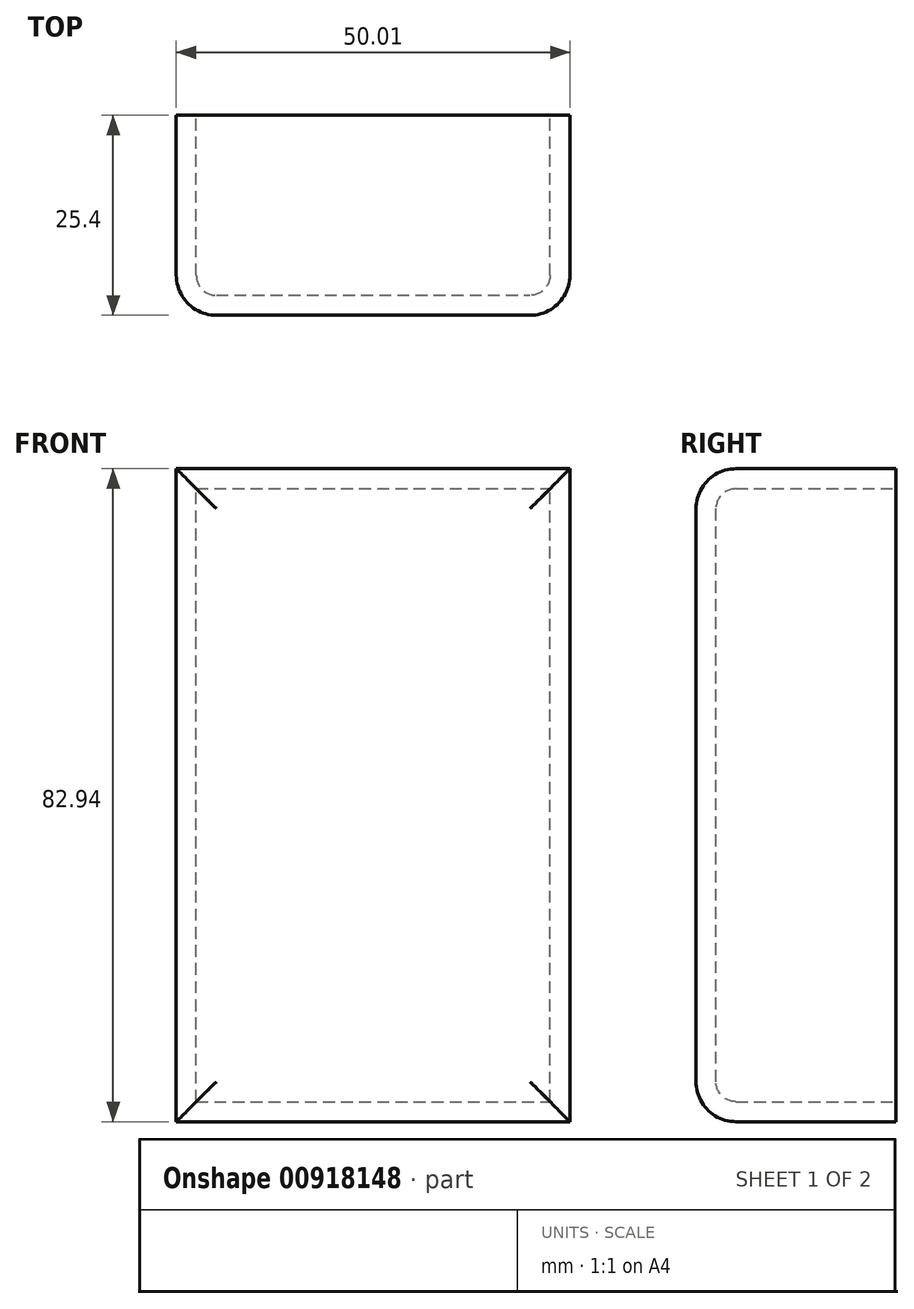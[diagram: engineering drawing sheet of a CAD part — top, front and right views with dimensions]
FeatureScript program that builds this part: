
annotation { "Feature Type Name" : "Feature", "Feature Type Description" : "" }
export const myFeature = defineFeature(function(context is Context, id is Id, definition is map)
    precondition{}
    {
        {
            var Q0;
            Q0=qCreatedBy(makeId("Front.planeOp"),FACE);
            var sketch = newSketch(context, id + "F0", { "sketchPlane" : qUnion([Q0])});
            skLineSegment(sketch, "E0.bottom", {"start": v(22.5, 37.5) * mm, "end": v(72.5, 37.5) * mm});
            skLineSegment(sketch, "E0.top", {"start": v(22.5, 120.44) * mm, "end": v(72.5, 120.44) * mm});
            skLineSegment(sketch, "E0.left", {"start": v(22.5, 37.5) * mm, "end": v(22.5, 120.44) * mm});
            skLineSegment(sketch, "E0.right", {"start": v(72.5, 37.5) * mm, "end": v(72.5, 120.44) * mm});
            skSolve(sketch);
        }
        {
            var Q0;
            Q0=makeQuery(id+"F0.imprint","IMPRINT",FACE,{"disambiguationData":[TD([[makeQuery(id+"F0.imprint","IMPRINT",EDGE,{"derivedFrom":sQuery(id+"F0.wireOp",EDGE,"E0.bottom")}),1.0]])]});
            var Q1;
            Q1 = qSketchRegion(id + "F0", true);
            extrude(context, id + "F1", {"entities" : qUnion([Q0, Q1]), "depth" : 25.4 * mm, "offsetDistance" : 25.4 * mm});
        }
        {
            var Q0;
            Q0=makeQuery(id+"F1.opExtrude","CAP_EDGE",EDGE,{"disambiguationData":[OSD([sQuery(id+"F0.wireOp",EDGE,"E0.right")])],"isStart":false});
            var Q1;
            Q1=makeQuery(id+"F1.opExtrude","CAP_EDGE",EDGE,{"disambiguationData":[OSD([sQuery(id+"F0.wireOp",EDGE,"E0.left")])],"isStart":false});
            var Q2;
            Q2=makeQuery(id+"F1.opExtrude","CAP_EDGE",EDGE,{"disambiguationData":[OSD([sQuery(id+"F0.wireOp",EDGE,"E0.top")])],"isStart":false});
            var Q3;
            Q3=makeQuery(id+"F1.opExtrude","CAP_EDGE",EDGE,{"disambiguationData":[OSD([sQuery(id+"F0.wireOp",EDGE,"E0.bottom")])],"isStart":false});
            fillet(context, id + "F2", {"entities" : qUnion([Q0, Q1, Q2, Q3]), "radius" : 5.08 * mm, "tangentPropagation" : true, "allowEdgeOverflow" : false});
        }
        {
            var Q0;
            Q0=makeQuery(id+"F1.opExtrude","CAP_FACE",FACE,{"disambiguationData":[OSD([sQuery(id+"F0.wireOp",EDGE,"E0.bottom"),sQuery(id+"F0.wireOp",EDGE,"E0.top"),sQuery(id+"F0.wireOp",EDGE,"E0.left"),sQuery(id+"F0.wireOp",EDGE,"E0.right")])],"isStart":true});
            shell(context, id + "F3", {"entities" : qUnion([Q0]), "thickness" : 2.54 * mm});
        }
        {
            var Q0;
            Q0=makeQuery(id+"F3.opShell","OFFSET_FACE",FACE,{"disambiguationData":[OSD([sQuery(id+"F0.wireOp",EDGE,"E0.bottom"),sQuery(id+"F0.wireOp",EDGE,"E0.top"),sQuery(id+"F0.wireOp",EDGE,"E0.left"),sQuery(id+"F0.wireOp",EDGE,"E0.right")])]});
            var sketch = newSketch(context, id + "F4", { "sketchPlane" : qUnion([Q0])});
            skCircle(sketch, "E1", {"center": v(-48.92, 74.95) * mm, "radius": 5.58 * mm});
            skCircle(sketch, "E2", {"center": v(-48.92, 74.95) * mm, "radius": 3.37 * mm});
            skSolve(sketch);
        }
        {
            var Q0;
            Q0=sQuery(id+"F4.wireOp",EDGE,"E1");
            var Q1;
            Q1=sQuery(id+"F4.wireOp",EDGE,"E2");
            var Q2;
            Q2=makeQuery(id+"F1.opExtrude","CAP_FACE",FACE,{"disambiguationData":[OSD([sQuery(id+"F0.wireOp",EDGE,"E0.bottom"),sQuery(id+"F0.wireOp",EDGE,"E0.top"),sQuery(id+"F0.wireOp",EDGE,"E0.left"),sQuery(id+"F0.wireOp",EDGE,"E0.right")])],"isStart":true});
            extrude(context, id + "F5", {"bodyType" : ToolBodyType.SURFACE, "surfaceEntities" : qUnion([Q0, Q1]), "endBound" : BoundingType.UP_TO_SURFACE, "depth" : 25.4 * mm, "endBoundEntityFace" : qUnion([Q2]), "offsetDistance" : 25.4 * mm});
        }
    });
